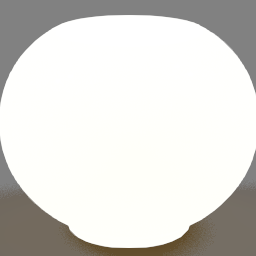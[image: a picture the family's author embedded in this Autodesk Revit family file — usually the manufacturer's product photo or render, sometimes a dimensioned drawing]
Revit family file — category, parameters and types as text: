
# Revit family: 3-010X-xx Avior Mirror
name_source: partatom
category: Lighting Fixtures
units: mm (PartAtom-declared; Revit-internal decimal feet)

## family parameters
Always vertical = Yes
Cut with Voids When Loaded = No
Host = Wall
Light Source = No
OmniClass Number = 23.80.70.00
OmniClass Title = Lighting
Part Type = Normal
Room Calculation Point = No
Round Connector Dimension = Use Diameter
Shared = No

## types (4) — shared parameters
Lamp = LED Array
Manufacturer = Vanita by Oxygen
Metal Finish 1 = 15 - Black
Model = 3-010X-xx / Avior Rectangle
References = Ref. 3 = 120 V / Ref. 37 = 277 V
URL = www.oxygenlighting.com
Voltage = 120 V
Voltage Input = 120 V or 277 V - 50/60 Hz
zero-valued in all types: Default Elevation

## per-type parameters (varying)
| type | Height | Wattage Comments | Width |
| 3-0101-15 / Black | 610 mm  [stored 2.00131 ft] | 1 x 26.7 W at 120 V | 457 mm  [stored 1.49934 ft] |
| 3-0102-15 / Black | 914 mm  [stored 2.99869 ft] | 1 x 50.8 W at 120 V | 610 mm  [stored 2.00131 ft] |
| 3-0103-15 / Black | 914 mm  [stored 2.99869 ft] | 1 x 58.7 W at 120 V | 610 mm  [stored 2.00131 ft] |
| 3-0104-15 / Black | 914 mm  [stored 2.99869 ft] | 1 x 72.3 W at 120 V | 610 mm  [stored 2.00131 ft] |

note: [stored X ft] marks values corroborated as IEEE doubles in the binary element streams (Revit-internal decimal feet)

## geometry (parser evidence)
native form markers: Sweep x5
no freeform markers — native parametric forms only
